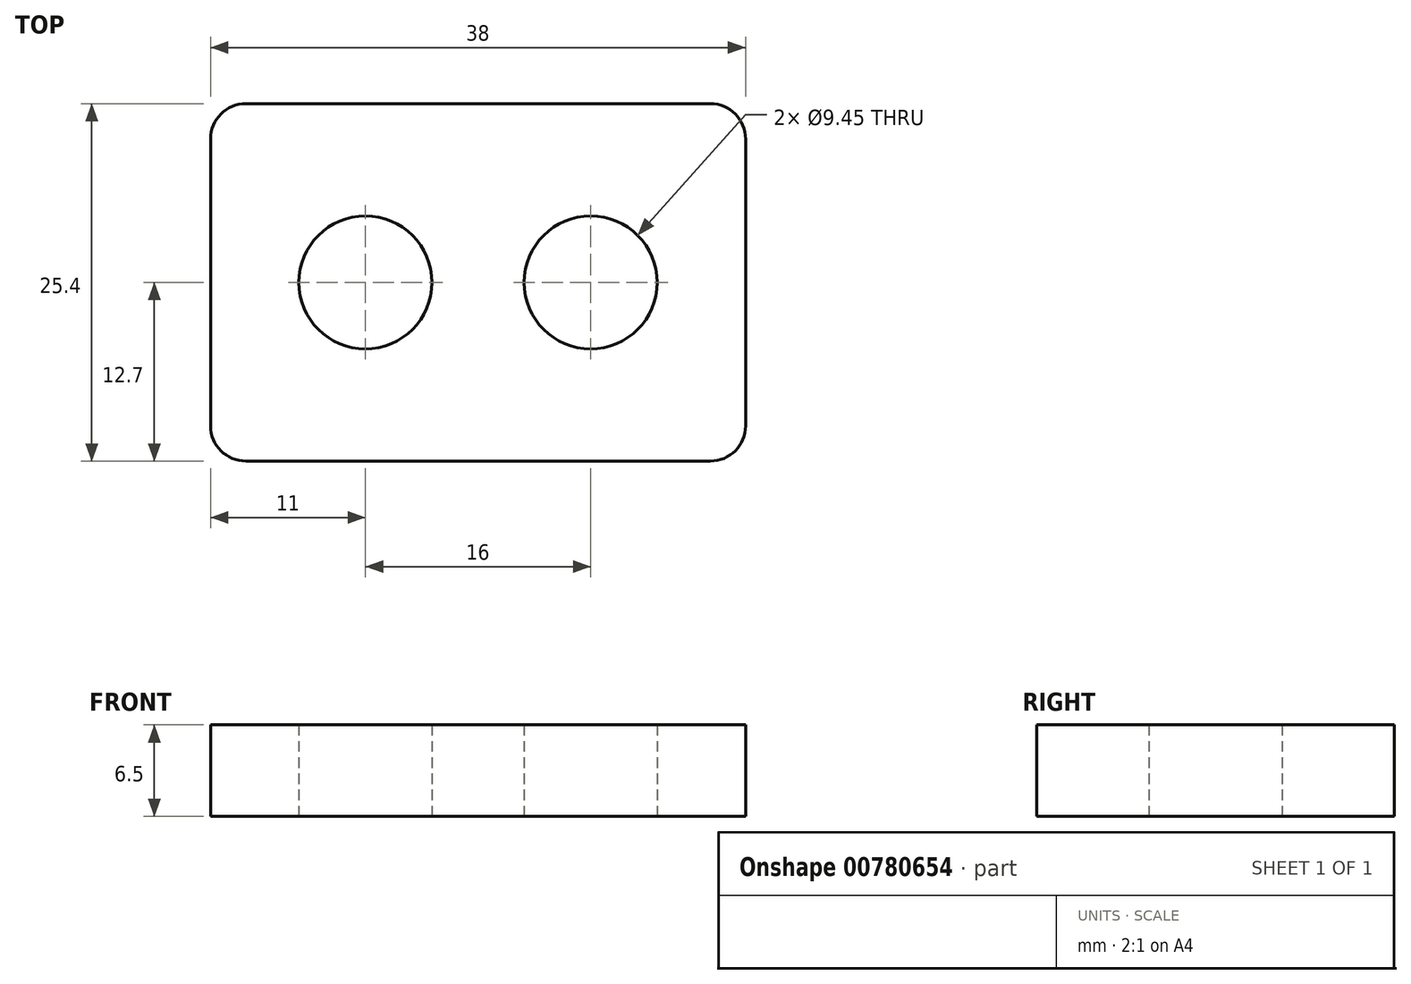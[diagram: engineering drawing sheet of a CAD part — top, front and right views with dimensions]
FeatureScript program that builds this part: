
annotation { "Feature Type Name" : "Feature", "Feature Type Description" : "" }
export const myFeature = defineFeature(function(context is Context, id is Id, definition is map)
    precondition{}
    {
        {
            var Q0;
            Q0=qCreatedBy(makeId("Top.planeOp"),FACE);
            var sketch = newSketch(context, id + "F0", { "sketchPlane" : qUnion([Q0])});
            skLineSegment(sketch, "E0.bottom", {"start": v(16.5, -12.7) * mm, "end": v(-16.5, -12.7) * mm});
            skLineSegment(sketch, "E0.top", {"start": v(16.5, 12.7) * mm, "end": v(-16.5, 12.7) * mm});
            skLineSegment(sketch, "E0.left", {"start": v(19, -10.2) * mm, "end": v(19, 10.2) * mm});
            skLineSegment(sketch, "E0.right", {"start": v(-19, -10.2) * mm, "end": v(-19, 10.2) * mm});
            skPoint(sketch, "E0.middle", {"position": v(0, 0) * mm});
            skLineSegment(sketch, "E1", {"start": v(0, 0) * mm, "end": v(8, 0) * mm});
            skLineSegment(sketch, "E2", {"start": v(0, 0) * mm, "end": v(-8, 0) * mm});
            skCircle(sketch, "E3", {"center": v(-8, 0) * mm, "radius": 4.72 * mm});
            skCircle(sketch, "E4", {"center": v(8, 0) * mm, "radius": 4.72 * mm});
            skPoint(sketch, "E5.visualSharp", {"position": v(-19, 12.7) * mm});
            skArc(sketch, "E5.filletArc", {"start": v(-16.5, 12.7) * mm, "mid": v(-18.27, 11.97) * mm, "end": v(-19, 10.2) * mm});
            skPoint(sketch, "E6.visualSharp", {"position": v(19, 12.7) * mm});
            skArc(sketch, "E6.filletArc", {"start": v(19, 10.2) * mm, "mid": v(18.27, 11.97) * mm, "end": v(16.5, 12.7) * mm});
            skPoint(sketch, "E7.visualSharp", {"position": v(19, -12.7) * mm});
            skArc(sketch, "E7.filletArc", {"start": v(16.5, -12.7) * mm, "mid": v(18.27, -11.97) * mm, "end": v(19, -10.2) * mm});
            skPoint(sketch, "E8.visualSharp", {"position": v(-19, -12.7) * mm});
            skArc(sketch, "E8.filletArc", {"start": v(-19, -10.2) * mm, "mid": v(-18.27, -11.97) * mm, "end": v(-16.5, -12.7) * mm});
            skSolve(sketch);
        }
        {
            var Q0;
            Q0=makeQuery(id+"F0.imprint","IMPRINT",FACE,{"disambiguationData":[TD([[makeQuery(id+"F0.imprint","IMPRINT",EDGE,{"derivedFrom":sQuery(id+"F0.wireOp",EDGE,"E0.bottom")}),-1.0]])]});
            extrude(context, id + "F1", {"entities" : qUnion([Q0]), "endBound" : BoundingType.SYMMETRIC, "depth" : 6.5 * mm, "offsetDistance" : 25 * mm});
        }
    });
